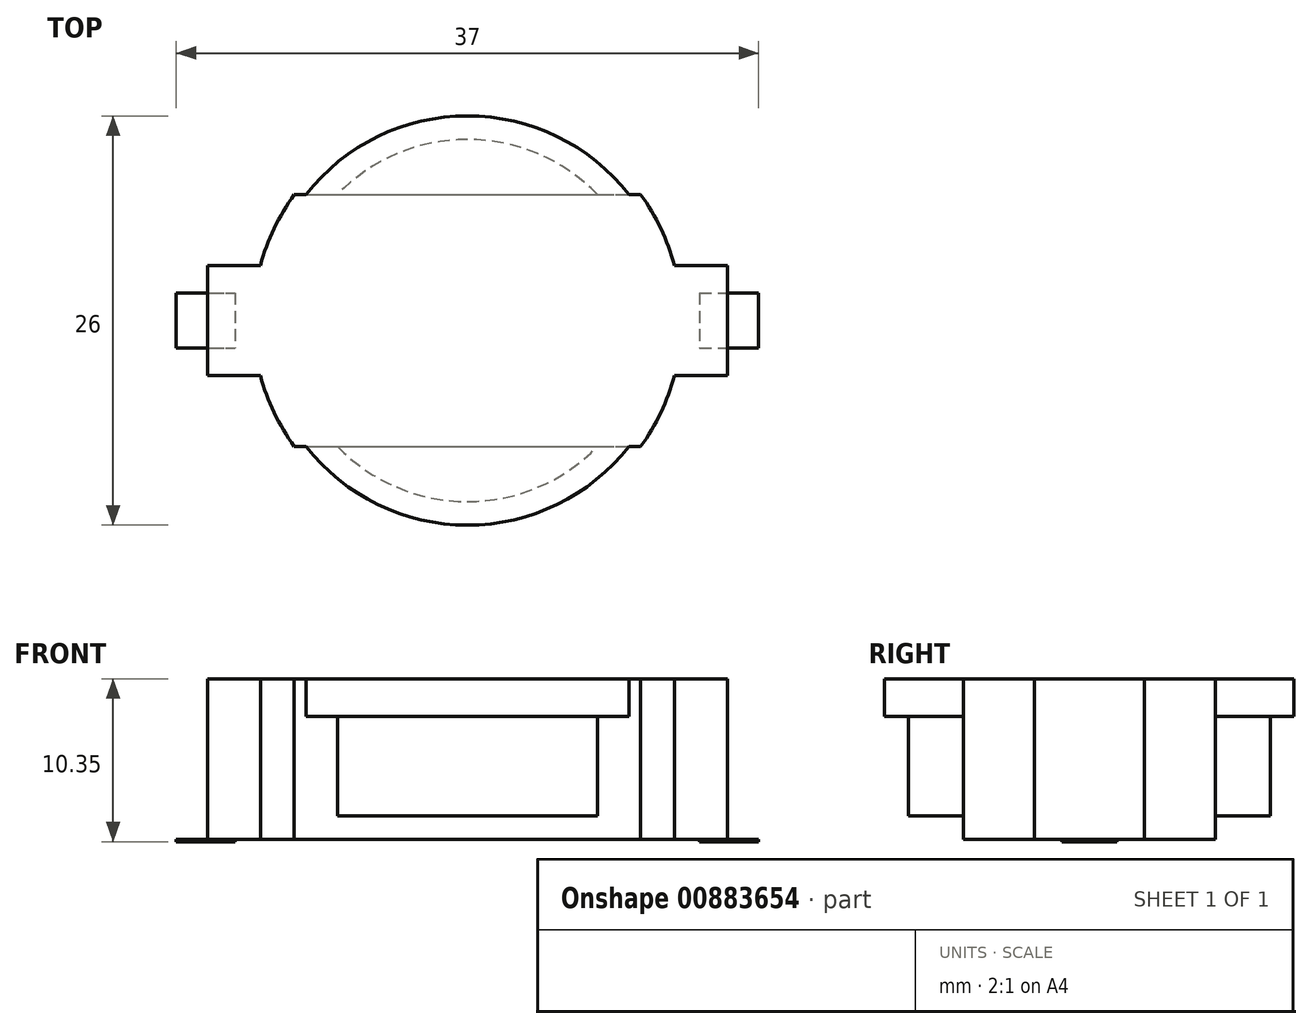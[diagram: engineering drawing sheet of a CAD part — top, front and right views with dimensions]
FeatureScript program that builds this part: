
annotation { "Feature Type Name" : "Feature", "Feature Type Description" : "" }
export const myFeature = defineFeature(function(context is Context, id is Id, definition is map)
    precondition{}
    {
        {
            var Q0;
            Q0=qCreatedBy(makeId("Top.planeOp"),FACE);
            var sketch = newSketch(context, id + "F0", { "sketchPlane" : qUnion([Q0])});
            skLineSegment(sketch, "E0.bottom", {"start": v(-18.5, 1.75) * mm, "end": v(-14.75, 1.75) * mm});
            skLineSegment(sketch, "E0.top", {"start": v(-18.5, -1.75) * mm, "end": v(-14.75, -1.75) * mm});
            skLineSegment(sketch, "E0.left", {"start": v(-18.5, 1.75) * mm, "end": v(-18.5, -1.75) * mm});
            skLineSegment(sketch, "E0.right", {"start": v(-14.75, 1.75) * mm, "end": v(-14.75, -1.75) * mm});
            skLineSegment(sketch, "E1.bottom", {"start": v(14.75, 1.75) * mm, "end": v(18.5, 1.75) * mm});
            skLineSegment(sketch, "E1.top", {"start": v(14.75, -1.75) * mm, "end": v(18.5, -1.75) * mm});
            skLineSegment(sketch, "E1.left", {"start": v(14.75, 1.75) * mm, "end": v(14.75, -1.75) * mm});
            skLineSegment(sketch, "E1.right", {"start": v(18.5, 1.75) * mm, "end": v(18.5, -1.75) * mm});
            skSolve(sketch);
        }
        {
            var Q0;
            Q0=makeQuery(id+"F0.imprint","IMPRINT",FACE,{"disambiguationData":[TD([[makeQuery(id+"F0.imprint","IMPRINT",EDGE,{"derivedFrom":sQuery(id+"F0.wireOp",EDGE,"E0.bottom")}),-1.0]])]});
            var Q1;
            Q1=makeQuery(id+"F0.imprint","IMPRINT",FACE,{"disambiguationData":[TD([[makeQuery(id+"F0.imprint","IMPRINT",EDGE,{"derivedFrom":sQuery(id+"F0.wireOp",EDGE,"E1.bottom")}),-1.0]])]});
            extrude(context, id + "F1", {"entities" : qUnion([Q0, Q1]), "depth" : 0.15 * mm, "offsetDistance" : 25 * mm});
        }
        {
            var Q0;
            Q0=makeQuery(id+"F1.opExtrude","CAP_FACE",FACE,{"disambiguationData":[OSD([sQuery(id+"F0.wireOp",EDGE,"E0.bottom"),sQuery(id+"F0.wireOp",EDGE,"E0.top"),sQuery(id+"F0.wireOp",EDGE,"E0.left"),sQuery(id+"F0.wireOp",EDGE,"E0.right")])],"isStart":false});
            var sketch = newSketch(context, id + "F2", { "sketchPlane" : qUnion([Q0])});
            skLineSegment(sketch, "E2.bottom", {"start": v(-16.5, 3.5) * mm, "end": v(16.5, 3.5) * mm});
            skLineSegment(sketch, "E2.top", {"start": v(-16.5, -3.5) * mm, "end": v(16.5, -3.5) * mm});
            skLineSegment(sketch, "E2.left", {"start": v(-16.5, 3.5) * mm, "end": v(-16.5, -3.5) * mm});
            skLineSegment(sketch, "E2.right", {"start": v(16.5, 3.5) * mm, "end": v(16.5, -3.5) * mm});
            skSolve(sketch);
        }
        {
            var Q0;
            Q0 = qSketchRegion(id + "F2", true);
            extrude(context, id + "F3", {"entities" : qUnion([Q0]), "depth" : 10.2 * mm, "offsetDistance" : 25 * mm});
        }
        {
            var Q0;
            Q0=makeQuery(id+"F1.opExtrude","CAP_FACE",FACE,{"disambiguationData":[OSD([sQuery(id+"F0.wireOp",EDGE,"E1.bottom"),sQuery(id+"F0.wireOp",EDGE,"E1.top"),sQuery(id+"F0.wireOp",EDGE,"E1.left"),sQuery(id+"F0.wireOp",EDGE,"E1.right")])],"isStart":false});
            var sketch = newSketch(context, id + "F4", { "sketchPlane" : qUnion([Q0])});
            skLineSegment(sketch, "E3", {"start": v(-11, 8) * mm, "end": v(11, 8) * mm});
            skLineSegment(sketch, "E4", {"start": v(-11, -8) * mm, "end": v(11, -8) * mm});
            skArc(sketch, "E5", {"start": v(-11, 8) * mm, "mid": v(-13.6, 0) * mm, "end": v(-11, -8) * mm});
            skArc(sketch, "E6", {"start": v(11, -8) * mm, "mid": v(13.6, 0) * mm, "end": v(11, 8) * mm});
            skSolve(sketch);
        }
        {
            var Q0;
            Q0=makeQuery(id+"F4.imprint","IMPRINT",FACE,{"disambiguationData":[TD([[makeQuery(id+"F4.imprint","IMPRINT",EDGE,{"derivedFrom":sQuery(id+"F4.wireOp",EDGE,"E3")}),-1.0]])]});
            extrude(context, id + "F5", {"entities" : qUnion([Q0]), "operationType" : NewBodyOperationType.ADD, "depth" : 10.2 * mm, "offsetDistance" : 25 * mm});
        }
        {
            var Q0;
            Q0=makeQuery(id+"F5.boolean.opBoolean","MERGE",FACE,{"derivedFrom":[makeQuery(id+"F3.opExtrude","CAP_FACE",FACE,{"disambiguationData":[OSD([sQuery(id+"F2.wireOp",EDGE,"E2.bottom"),sQuery(id+"F2.wireOp",EDGE,"E2.top"),sQuery(id+"F2.wireOp",EDGE,"E2.left"),sQuery(id+"F2.wireOp",EDGE,"E2.right")])],"isStart":false}),makeQuery(id+"F5.opExtrude","CAP_FACE",FACE,{"disambiguationData":[OSD([sQuery(id+"F4.wireOp",EDGE,"E3"),sQuery(id+"F4.wireOp",EDGE,"E4"),sQuery(id+"F4.wireOp",EDGE,"E5"),sQuery(id+"F4.wireOp",EDGE,"E6")])],"isStart":false})]});
            var sketch = newSketch(context, id + "F6", { "sketchPlane" : qUnion([Q0])});
            skCircle(sketch, "E7", {"center": v(0, 0) * mm, "radius": 11.5 * mm});
            skSolve(sketch);
        }
        {
            var Q0;
            Q0 = qSketchRegion(id + "F6", true);
            extrude(context, id + "F7", {"entities" : qUnion([Q0]), "operationType" : NewBodyOperationType.ADD, "oppositeDirection" : true, "depth" : 8.7 * mm, "offsetDistance" : 25 * mm});
        }
        {
            var Q0;
            Q0=makeQuery(id+"F7.boolean.opBoolean","MERGE",FACE,{"derivedFrom":[makeQuery(id+"F5.boolean.opBoolean","MERGE",FACE,{"derivedFrom":[makeQuery(id+"F3.opExtrude","CAP_FACE",FACE,{"disambiguationData":[OSD([sQuery(id+"F2.wireOp",EDGE,"E2.bottom"),sQuery(id+"F2.wireOp",EDGE,"E2.top"),sQuery(id+"F2.wireOp",EDGE,"E2.left"),sQuery(id+"F2.wireOp",EDGE,"E2.right")])],"isStart":false}),makeQuery(id+"F5.opExtrude","CAP_FACE",FACE,{"disambiguationData":[OSD([sQuery(id+"F4.wireOp",EDGE,"E3"),sQuery(id+"F4.wireOp",EDGE,"E4"),sQuery(id+"F4.wireOp",EDGE,"E5"),sQuery(id+"F4.wireOp",EDGE,"E6")])],"isStart":false})]}),makeQuery(id+"F7.opExtrude","CAP_FACE",FACE,{"disambiguationData":[OSD([sQuery(id+"F6.wireOp",EDGE,"E7")])],"isStart":true})]});
            var sketch = newSketch(context, id + "F8", { "sketchPlane" : qUnion([Q0])});
            skCircle(sketch, "E8", {"center": v(0, 0) * mm, "radius": 13 * mm});
            skSolve(sketch);
        }
        {
            var Q0;
            Q0 = qSketchRegion(id + "F8", true);
            extrude(context, id + "F9", {"entities" : qUnion([Q0]), "operationType" : NewBodyOperationType.ADD, "oppositeDirection" : true, "depth" : 2.4 * mm, "offsetDistance" : 25 * mm});
        }
    });
